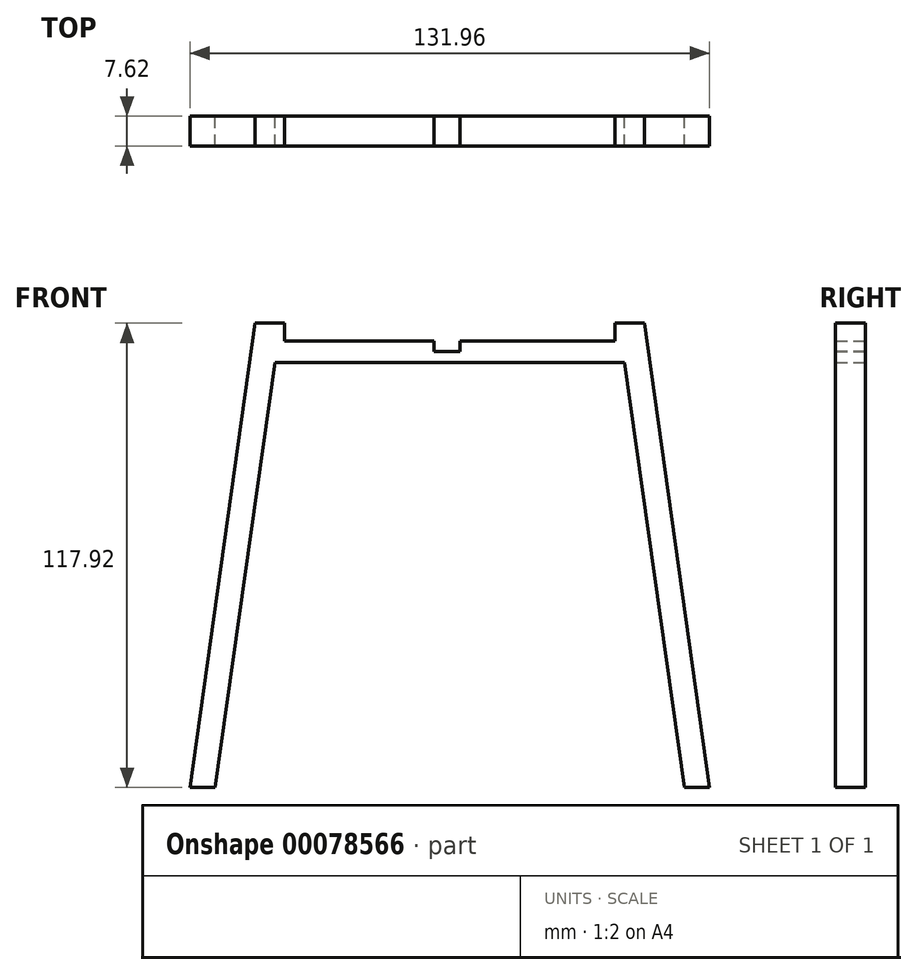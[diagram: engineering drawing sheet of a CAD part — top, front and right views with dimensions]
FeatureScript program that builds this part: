
annotation { "Feature Type Name" : "Feature", "Feature Type Description" : "" }
export const myFeature = defineFeature(function(context is Context, id is Id, definition is map)
    precondition{}
    {
        {
            var Q0;
            Q0=qCreatedBy(makeId("Front.planeOp"),FACE);
            var sketch = newSketch(context, id + "F0", { "sketchPlane" : qUnion([Q0])});
            skLineSegment(sketch, "E0", {"start": v(-65.98, -76.06) * mm, "end": v(-59.61, -76.06) * mm});
            skLineSegment(sketch, "E1", {"start": v(-59.61, -76.06) * mm, "end": v(-44.43, 31.94) * mm});
            skLineSegment(sketch, "E2", {"start": v(-44.43, 31.94) * mm, "end": v(0, 31.94) * mm});
            skLineSegment(sketch, "E3", {"start": v(-65.98, -76.06) * mm, "end": v(-49.4, 41.86) * mm});
            skLineSegment(sketch, "E4", {"start": v(-49.4, 41.86) * mm, "end": v(-41.97, 41.86) * mm});
            skLineSegment(sketch, "E5", {"start": v(-41.97, 41.86) * mm, "end": v(-41.97, 37.28) * mm});
            skLineSegment(sketch, "E6", {"start": v(-41.97, 37.28) * mm, "end": v(2.05, 37.28) * mm});
            skLineSegment(sketch, "E7.MirrorCS", {"start": v(65.98, -76.06) * mm, "end": v(59.61, -76.06) * mm});
            skLineSegment(sketch, "E8.MirrorCS", {"start": v(49.4, 41.86) * mm, "end": v(41.97, 41.86) * mm});
            skLineSegment(sketch, "E9.MirrorCS", {"start": v(41.97, 41.86) * mm, "end": v(41.97, 37.28) * mm});
            skLineSegment(sketch, "E10.MirrorCS", {"start": v(59.61, -76.06) * mm, "end": v(44.43, 31.94) * mm});
            skLineSegment(sketch, "E11.MirrorCS", {"start": v(65.98, -76.06) * mm, "end": v(49.4, 41.86) * mm});
            skLineSegment(sketch, "E12.MirrorCS", {"start": v(44.43, 31.94) * mm, "end": v(0, 31.94) * mm});
            skLineSegment(sketch, "E13.MirrorCS", {"start": v(41.97, 37.28) * mm, "end": v(2.05, 37.28) * mm});
            skLineSegment(sketch, "E14", {"start": v(-59.61, -76.06) * mm, "end": v(37.75, -76.06) * mm});
            skPoint(sketch, "E15.orphan", {"position": v(-2.05, 37.28) * mm});
            skSolve(sketch);
        }
        {
            var Q0;
            Q0=makeQuery(id+"F0.imprint","IMPRINT",FACE,{"disambiguationData":[TD([[makeQuery(id+"F0.imprint","IMPRINT",EDGE,{"derivedFrom":sQuery(id+"F0.wireOp",EDGE,"E0")}),1.0]])]});
            extrude(context, id + "F1", {"entities" : qUnion([Q0]), "depth" : 7.62 * mm});
        }
        {
            var Q0;
            Q0=qCreatedBy(makeId("Front.planeOp"),FACE);
            var sketch = newSketch(context, id + "F2", { "sketchPlane" : qUnion([Q0])});
            skLineSegment(sketch, "E16.top", {"start": v(-2.7, 34.62) * mm, "end": v(2.64, 34.62) * mm});
            skLineSegment(sketch, "E16.left", {"start": v(-2.7, 37.28) * mm, "end": v(-2.7, 34.62) * mm});
            skLineSegment(sketch, "E16.right", {"start": v(2.64, 37.28) * mm, "end": v(2.64, 34.62) * mm});
            skLineSegment(sketch, "E17", {"start": v(-2.7, 37.28) * mm, "end": v(2.64, 37.28) * mm});
            skSolve(sketch);
        }
        {
            var Q0;
            Q0=makeQuery(id+"F2.imprint","IMPRINT",FACE,{"disambiguationData":[TD([[makeQuery(id+"F2.imprint","IMPRINT",EDGE,{"derivedFrom":sQuery(id+"F2.wireOp",EDGE,"E16.top")}),1.0]])]});
            var Q1;
            Q1 = qSketchRegion(id + "F5", true);
            extrude(context, id + "F3", {"entities" : qUnion([Q0, Q1]), "operationType" : NewBodyOperationType.REMOVE, "depth" : 7.9 * mm});
        }
        {
            var Q0;
            Q0=qCreatedBy(makeId("Front.planeOp"),FACE);
            var sketch = newSketch(context, id + "F4", { "sketchPlane" : qUnion([Q0])});
            skLineSegment(sketch, "E18.bottom", {"start": v(-4.06, 37.28) * mm, "end": v(-2.7, 37.28) * mm});
            skLineSegment(sketch, "E18.top", {"start": v(-4.06, 34.63) * mm, "end": v(-2.7, 34.63) * mm});
            skLineSegment(sketch, "E18.left", {"start": v(-4.06, 37.28) * mm, "end": v(-4.06, 34.63) * mm});
            skLineSegment(sketch, "E18.right", {"start": v(-2.7, 37.28) * mm, "end": v(-2.7, 34.63) * mm});
            skSolve(sketch);
        }
        {
            var Q0;
            Q0=makeQuery(id+"F3.boolean.opBoolean","COPY",FACE,{"derivedFrom":makeQuery(id+"F3.opExtrude","SWEPT_FACE",FACE,{"disambiguationData":[OSD([sQuery(id+"F2.wireOp",EDGE,"E16.left")])]})});
            var sketch = newSketch(context, id + "F5", { "sketchPlane" : qUnion([Q0])});
            skSolve(sketch);
        }
        {
            var Q0;
            Q0 = qSketchRegion(id + "F4", true);
            extrude(context, id + "F6", {"entities" : qUnion([Q0]), "operationType" : NewBodyOperationType.REMOVE, "depth" : 36.45 * mm});
        }
    });
